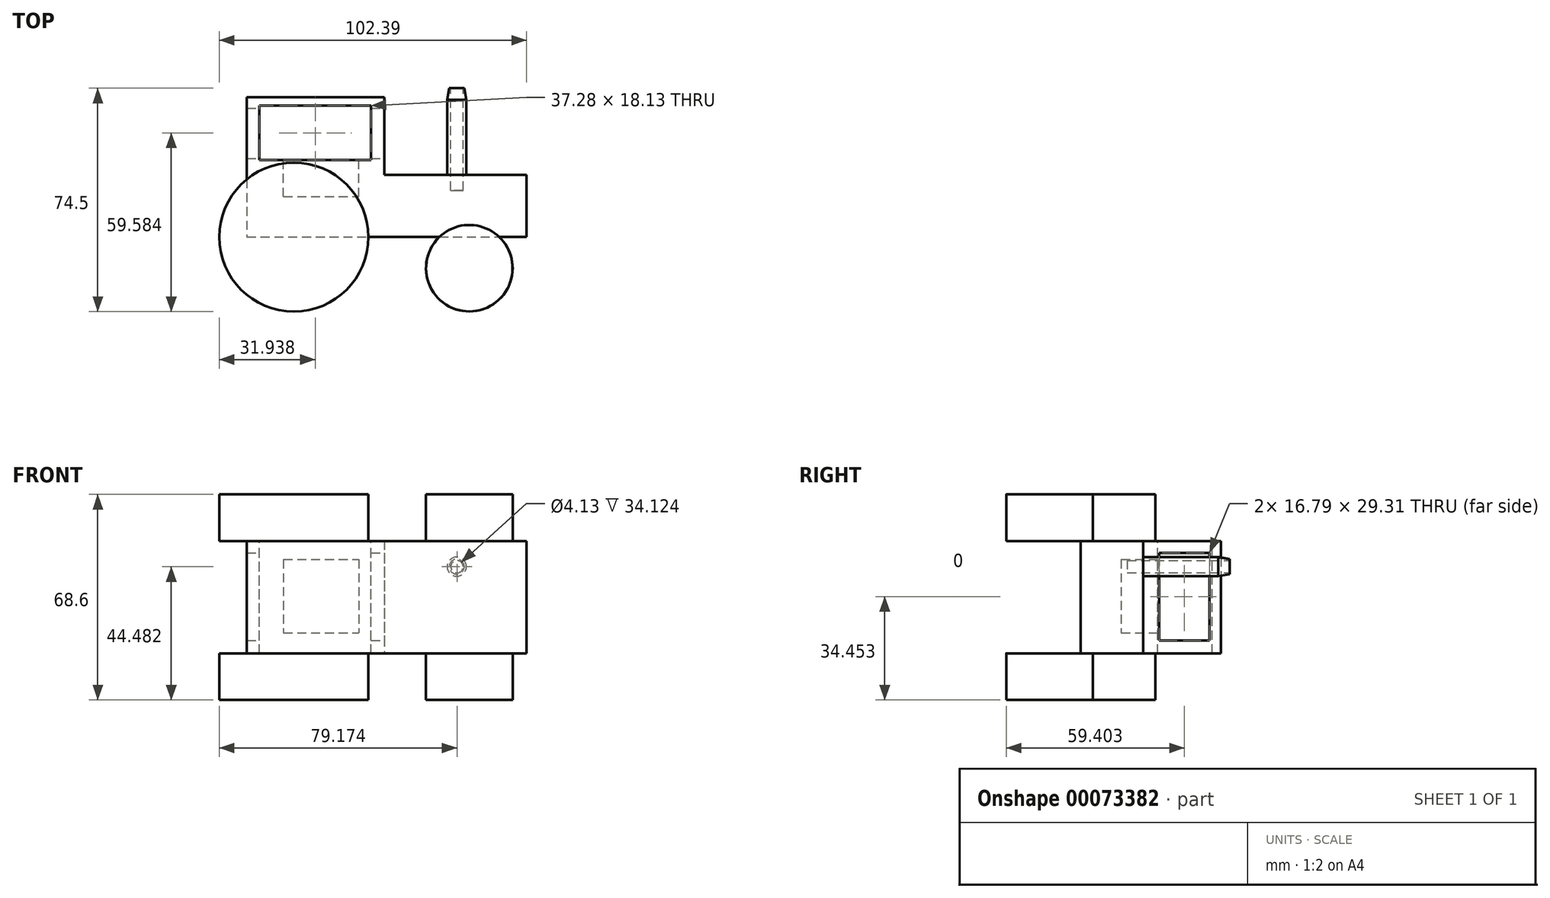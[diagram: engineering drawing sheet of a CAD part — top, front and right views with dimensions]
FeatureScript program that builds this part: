
annotation { "Feature Type Name" : "Feature", "Feature Type Description" : "" }
export const myFeature = defineFeature(function(context is Context, id is Id, definition is map)
    precondition{}
    {
        {
            var Q0;
            Q0=qCreatedBy(makeId("Top.planeOp"),FACE);
            var sketch = newSketch(context, id + "F0", { "sketchPlane" : qUnion([Q0])});
            skLineSegment(sketch, "E0.bottom", {"start": v(-51.46, 51.22) * mm, "end": v(-5.58, 51.22) * mm});
            skLineSegment(sketch, "E0.top", {"start": v(-51.46, 4.52) * mm, "end": v(-5.58, 4.52) * mm});
            skLineSegment(sketch, "E0.left", {"start": v(-51.46, 51.22) * mm, "end": v(-51.46, 4.52) * mm});
            skLineSegment(sketch, "E0.right", {"start": v(-5.58, 51.22) * mm, "end": v(-5.58, 25.29) * mm});
            skLineSegment(sketch, "E1.bottom", {"start": v(-5.58, 4.52) * mm, "end": v(41.8, 4.52) * mm});
            skLineSegment(sketch, "E1.top", {"start": v(-5.58, 25.29) * mm, "end": v(41.8, 25.29) * mm});
            skLineSegment(sketch, "E1.right", {"start": v(41.8, 4.52) * mm, "end": v(41.8, 25.29) * mm});
            skSolve(sketch);
        }
        {
            var Q0;
            Q0=makeQuery(id+"F0.imprint","IMPRINT",FACE,{"disambiguationData":[TD([[makeQuery(id+"F0.imprint","IMPRINT",EDGE,{"derivedFrom":sQuery(id+"F0.wireOp",EDGE,"E0.bottom")}),-1.0]])]});
            extrude(context, id + "F1", {"entities" : qUnion([Q0]), "endBound" : BoundingType.SYMMETRIC, "depth" : 37.5 * mm});
        }
        {
            var Q0;
            Q0=makeQuery(id+"F1.opExtrude","CAP_FACE",FACE,{"disambiguationData":[OSD([sQuery(id+"F0.wireOp",EDGE,"E0.bottom"),sQuery(id+"F0.wireOp",EDGE,"E0.top"),sQuery(id+"F0.wireOp",EDGE,"E0.left"),sQuery(id+"F0.wireOp",EDGE,"E0.right"),sQuery(id+"F0.wireOp",EDGE,"E1.bottom"),sQuery(id+"F0.wireOp",EDGE,"E1.top"),sQuery(id+"F0.wireOp",EDGE,"E1.right")])],"isStart":false});
            var sketch = newSketch(context, id + "F2", { "sketchPlane" : qUnion([Q0])});
            skCircle(sketch, "E2", {"center": v(-35.77, 4.52) * mm, "radius": 24.83 * mm});
            skCircle(sketch, "E3", {"center": v(22.7, -5.87) * mm, "radius": 14.42 * mm});
            skLineSegment(sketch, "E4", {"start": v(-36.74, -20.29) * mm, "end": v(62.88, -20.29) * mm, "construction": true});
            skSolve(sketch);
        }
        {
            var Q0;
            {var subQ0=sQuery(id+"F2.wireOp",EDGE,"E2");var subQ3=makeQuery(id+"F1.opExtrude","CAP_EDGE",EDGE,{"disambiguationData":[OSD([sQuery(id+"F0.wireOp",EDGE,"E0.left")])],"isStart":false});var subQ4=makeQuery(id+"F2.imprint","INTERSECT",VERTEX,{"derivedFrom":[subQ3,subQ0]});Q0=makeQuery(id+"F2.imprint","IMPRINT",FACE,{"disambiguationData":[TD([[makeQuery(id+"F2.imprint","IMPRINT",EDGE,{"disambiguationData":[TD([[subQ4,-1.0]])],"derivedFrom":subQ0}),1.0]])]});}
            var Q1;
            {var subQ0=sQuery(id+"F2.wireOp",EDGE,"E2");var subQ3=makeQuery(id+"F1.opExtrude","CAP_EDGE",EDGE,{"disambiguationData":[OSD([sQuery(id+"F0.wireOp",EDGE,"E0.left")])],"isStart":false});var subQ4=makeQuery(id+"F2.imprint","INTERSECT",VERTEX,{"derivedFrom":[subQ3,subQ0]});Q1=makeQuery(id+"F2.imprint","IMPRINT",FACE,{"disambiguationData":[TD([[makeQuery(id+"F2.imprint","IMPRINT",EDGE,{"disambiguationData":[TD([[subQ4,1.0]])],"derivedFrom":subQ0}),1.0]])]});}
            var Q2;
            {var subQ0=sQuery(id+"F2.wireOp",EDGE,"E3");var subQ1=makeQuery(id+"F1.opExtrude","CAP_EDGE",EDGE,{"disambiguationData":[OSD([sQuery(id+"F0.wireOp",EDGE,"E0.top"),sQuery(id+"F0.wireOp",EDGE,"E1.bottom")])],"isStart":false});var subQ2=makeQuery(id+"F2.imprint","INTERSECT",VERTEX,{"disambiguationData":[OD(0.0)],"derivedFrom":[subQ1,subQ0]});Q2=makeQuery(id+"F2.imprint","IMPRINT",FACE,{"disambiguationData":[TD([[makeQuery(id+"F2.imprint","IMPRINT",EDGE,{"disambiguationData":[TD([[subQ2,1.0]])],"derivedFrom":subQ0}),1.0]])]});}
            var Q3;
            {var subQ0=sQuery(id+"F2.wireOp",EDGE,"E3");var subQ1=makeQuery(id+"F1.opExtrude","CAP_EDGE",EDGE,{"disambiguationData":[OSD([sQuery(id+"F0.wireOp",EDGE,"E0.top"),sQuery(id+"F0.wireOp",EDGE,"E1.bottom")])],"isStart":false});var subQ2=makeQuery(id+"F2.imprint","INTERSECT",VERTEX,{"disambiguationData":[OD(0.0)],"derivedFrom":[subQ1,subQ0]});Q3=makeQuery(id+"F2.imprint","IMPRINT",FACE,{"disambiguationData":[TD([[makeQuery(id+"F2.imprint","IMPRINT",EDGE,{"disambiguationData":[TD([[subQ2,-1.0]])],"derivedFrom":subQ0}),1.0]])]});}
            extrude(context, id + "F3", {"entities" : qUnion([Q0, Q1, Q2, Q3]), "operationType" : NewBodyOperationType.ADD, "depth" : 15.55 * mm});
        }
        {
            var Q0;
            Q0=makeQuery(id+"F1.opExtrude","SWEPT_BODY",BODY,{"disambiguationData":[OSD([sQuery(id+"F0.wireOp",EDGE,"E0.bottom"),sQuery(id+"F0.wireOp",EDGE,"E0.top"),sQuery(id+"F0.wireOp",EDGE,"E0.left"),sQuery(id+"F0.wireOp",EDGE,"E0.right"),sQuery(id+"F0.wireOp",EDGE,"E1.bottom"),sQuery(id+"F0.wireOp",EDGE,"E1.top"),sQuery(id+"F0.wireOp",EDGE,"E1.right")])]});
            var Q1;
            Q1=qCreatedBy(makeId("Top.planeOp"),FACE);
            mirror(context, id + "F4", {"operationType" : NewBodyOperationType.ADD, "entities" : qUnion([Q0]), "mirrorPlane" : qUnion([Q1])});
        }
        {
            var Q0;
            Q0=makeQuery(id+"F1.opExtrude","CAP_FACE",FACE,{"disambiguationData":[OSD([sQuery(id+"F0.wireOp",EDGE,"E0.bottom"),sQuery(id+"F0.wireOp",EDGE,"E0.top"),sQuery(id+"F0.wireOp",EDGE,"E0.left"),sQuery(id+"F0.wireOp",EDGE,"E0.right"),sQuery(id+"F0.wireOp",EDGE,"E1.bottom"),sQuery(id+"F0.wireOp",EDGE,"E1.top"),sQuery(id+"F0.wireOp",EDGE,"E1.right")])],"isStart":false});
            var sketch = newSketch(context, id + "F5", { "sketchPlane" : qUnion([Q0])});
            skLineSegment(sketch, "E5.bottom", {"start": v(-47.3, 48.34) * mm, "end": v(-10.02, 48.34) * mm});
            skLineSegment(sketch, "E5.top", {"start": v(-47.3, 30.2) * mm, "end": v(-10.02, 30.2) * mm});
            skLineSegment(sketch, "E5.left", {"start": v(-47.3, 48.34) * mm, "end": v(-47.3, 30.2) * mm});
            skLineSegment(sketch, "E5.right", {"start": v(-10.02, 48.34) * mm, "end": v(-10.02, 30.2) * mm});
            skSolve(sketch);
        }
        {
            var Q0;
            Q0=makeQuery(id+"F5.imprint","IMPRINT",FACE,{"disambiguationData":[TD([[makeQuery(id+"F5.imprint","IMPRINT",EDGE,{"derivedFrom":sQuery(id+"F5.wireOp",EDGE,"E5.bottom")}),-1.0]])]});
            extrude(context, id + "F6", {"entities" : qUnion([Q0]), "operationType" : NewBodyOperationType.REMOVE, "endBound" : BoundingType.THROUGH_ALL, "oppositeDirection" : true, "depth" : 25 * mm});
        }
        {
            var Q0;
            Q0=makeQuery(id+"F1.opExtrude","SWEPT_FACE",FACE,{"disambiguationData":[OSD([sQuery(id+"F0.wireOp",EDGE,"E0.right")])]});
            var sketch = newSketch(context, id + "F7", { "sketchPlane" : qUnion([Q0])});
            skLineSegment(sketch, "E6.bottom", {"start": v(47.49, 14.8) * mm, "end": v(30.7, 14.8) * mm});
            skLineSegment(sketch, "E6.top", {"start": v(47.49, -14.5) * mm, "end": v(30.7, -14.5) * mm});
            skLineSegment(sketch, "E6.left", {"start": v(47.49, 14.8) * mm, "end": v(47.49, -14.5) * mm});
            skLineSegment(sketch, "E6.right", {"start": v(30.7, 14.8) * mm, "end": v(30.7, -14.5) * mm});
            skSolve(sketch);
        }
        {
            var Q0;
            Q0=makeQuery(id+"F7.imprint","IMPRINT",FACE,{"disambiguationData":[TD([[makeQuery(id+"F7.imprint","IMPRINT",EDGE,{"derivedFrom":sQuery(id+"F7.wireOp",EDGE,"E6.bottom")}),1.0]])]});
            extrude(context, id + "F8", {"entities" : qUnion([Q0]), "operationType" : NewBodyOperationType.REMOVE, "endBound" : BoundingType.THROUGH_ALL, "oppositeDirection" : true, "depth" : 25 * mm});
        }
        {
            var Q0;
            Q0=makeQuery(id+"F1.opExtrude","SWEPT_FACE",FACE,{"disambiguationData":[OSD([sQuery(id+"F0.wireOp",EDGE,"E1.top")])]});
            var sketch = newSketch(context, id + "F9", { "sketchPlane" : qUnion([Q0])});
            skCircle(sketch, "E7", {"center": v(-18.5, 10.19) * mm, "radius": 3.2 * mm});
            skSolve(sketch);
        }
        {
            var Q0;
            Q0=makeQuery(id+"F9.imprint","IMPRINT",FACE,{"disambiguationData":[TD([[makeQuery(id+"F9.imprint","IMPRINT",EDGE,{"derivedFrom":sQuery(id+"F9.wireOp",EDGE,"E7")}),1.0]])]});
            extrude(context, id + "F10", {"entities" : qUnion([Q0]), "operationType" : NewBodyOperationType.ADD, "depth" : 25 * mm});
        }
        {
            var Q0;
            Q0=makeQuery(id+"F10.opExtrude","CAP_FACE",FACE,{"disambiguationData":[OSD([sQuery(id+"F9.wireOp",EDGE,"E7")])],"isStart":false});
            var sketch = newSketch(context, id + "F11", { "sketchPlane" : qUnion([Q0])});
            skSolve(sketch);
        }
        {
            var Q0;
            Q0=makeQuery(id+"F11.imprint","IMPRINT",FACE,{"disambiguationData":[TD([[makeQuery(id+"F11.imprint","IMPRINT",EDGE,{"derivedFrom":makeQuery(id+"F10.opExtrude","CAP_EDGE",EDGE,{"disambiguationData":[OSD([sQuery(id+"F9.wireOp",EDGE,"E7")])],"isStart":false})}),1.0]])]});
            var sketch = newSketch(context, id + "F12", { "sketchPlane" : qUnion([Q0])});
            skSolve(sketch);
        }
        {
            var Q0;
            Q0 = qSketchRegion(id + "F12", true);
            var Q1;
            Q1=makeQuery(id+"F11.imprint","IMPRINT",FACE,{"disambiguationData":[TD([[makeQuery(id+"F11.imprint","IMPRINT",EDGE,{"derivedFrom":makeQuery(id+"F10.opExtrude","CAP_EDGE",EDGE,{"disambiguationData":[OSD([sQuery(id+"F9.wireOp",EDGE,"E7")])],"isStart":false})}),1.0]])]});
            extrude(context, id + "F13", {"entities" : qUnion([Q0, Q1]), "operationType" : NewBodyOperationType.ADD, "depth" : 3.9 * mm, "hasDraft" : true, "draftAngle" : 10 * degree, "draftPullDirection" : true});
        }
        {
            var Q0;
            Q0=makeQuery(id+"F6.boolean.opBoolean","COPY",FACE,{"derivedFrom":makeQuery(id+"F6.opExtrude","SWEPT_FACE",FACE,{"disambiguationData":[OSD([sQuery(id+"F5.wireOp",EDGE,"E5.top")])]})});
            var sketch = newSketch(context, id + "F14", { "sketchPlane" : qUnion([Q0])});
            skLineSegment(sketch, "E8.bottom", {"start": v(39.24, 12.58) * mm, "end": v(14.19, 12.58) * mm});
            skLineSegment(sketch, "E8.top", {"start": v(39.24, -11.92) * mm, "end": v(14.19, -11.92) * mm});
            skLineSegment(sketch, "E8.left", {"start": v(39.24, 12.58) * mm, "end": v(39.24, -11.92) * mm});
            skLineSegment(sketch, "E8.right", {"start": v(14.19, 12.58) * mm, "end": v(14.19, -11.92) * mm});
            skSolve(sketch);
        }
        {
            var Q0;
            Q0=makeQuery(id+"F14.imprint","IMPRINT",FACE,{"disambiguationData":[TD([[makeQuery(id+"F14.imprint","IMPRINT",EDGE,{"derivedFrom":sQuery(id+"F14.wireOp",EDGE,"E8.bottom")}),1.0]])]});
            extrude(context, id + "F18", {"entities" : qUnion([Q0]), "operationType" : NewBodyOperationType.REMOVE, "oppositeDirection" : true, "depth" : 12.2 * mm});
        }
        {
            var Q0;
            Q0=makeQuery(id+"F13.opExtrude","CAP_FACE",FACE,{"disambiguationData":[OSD([sQuery(id+"F9.wireOp",EDGE,"E7")])],"isStart":false});
            var sketch = newSketch(context, id + "F15", { "sketchPlane" : qUnion([Q0])});
            skSolve(sketch);
        }
        {
            var Q0;
            Q0=makeQuery(id+"F15.imprint","IMPRINT",FACE,{"disambiguationData":[TD([[makeQuery(id+"F15.imprint","IMPRINT",EDGE,{"derivedFrom":makeQuery(id+"F13.opExtrude","CAP_EDGE",EDGE,{"disambiguationData":[OSD([sQuery(id+"F9.wireOp",EDGE,"E7")])],"isStart":false})}),1.0]])]});
            var sketch = newSketch(context, id + "F16", { "sketchPlane" : qUnion([Q0])});
            skCircle(sketch, "E9", {"center": v(-18.57, 10.18) * mm, "radius": 2.06 * mm});
            skSolve(sketch);
        }
        {
            var Q0;
            Q0 = qSketchRegion(id + "F16", true);
            extrude(context, id + "F17", {"entities" : qUnion([Q0]), "operationType" : NewBodyOperationType.REMOVE, "oppositeDirection" : true, "depth" : 34.12 * mm});
        }
    });
